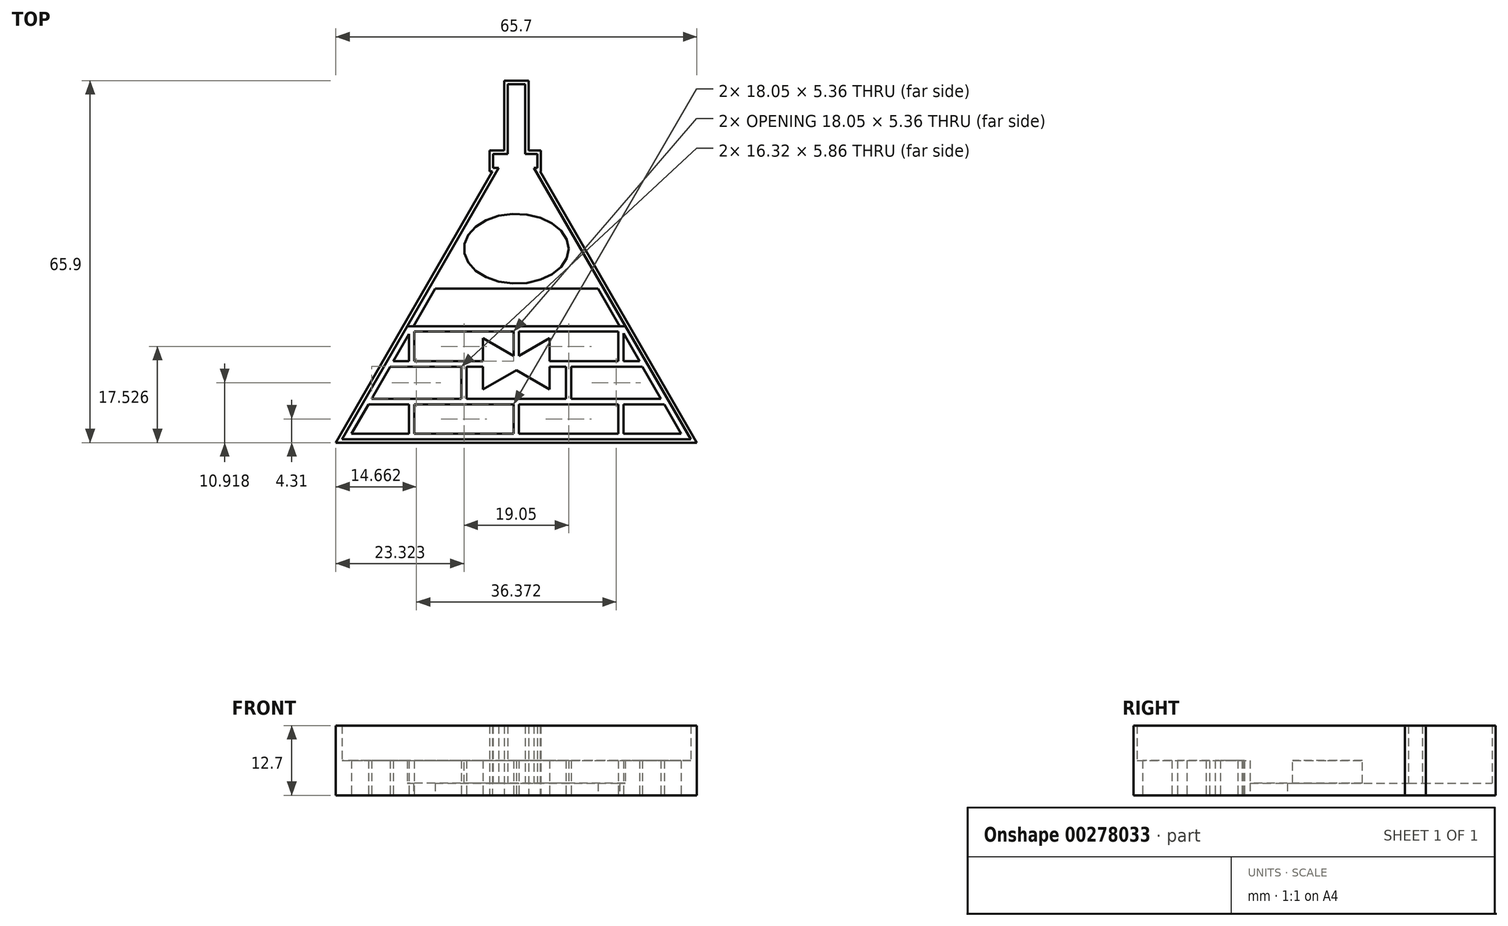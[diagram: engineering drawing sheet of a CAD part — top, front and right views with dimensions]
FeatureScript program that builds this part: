
annotation { "Feature Type Name" : "Feature", "Feature Type Description" : "" }
export const myFeature = defineFeature(function(context is Context, id is Id, definition is map)
    precondition{}
    {
        {
            var Q0;
            Q0=qCreatedBy(makeId("Top.planeOp"),FACE);
            var sketch = newSketch(context, id + "F0", { "sketchPlane" : qUnion([Q0])});
            skLineSegment(sketch, "E0", {"start": v(-57.59, 40.25) * mm, "end": v(-86.1, -9.14) * mm});
            skLineSegment(sketch, "E1", {"start": v(-86.1, -9.14) * mm, "end": v(-22.6, -9.14) * mm});
            skLineSegment(sketch, "E2", {"start": v(-22.6, -9.14) * mm, "end": v(-51.12, 40.25) * mm});
            skEllipse(sketch, "E3", {"center": v(-54.35, 25.53) * mm, "majorRadius": 6.35 * mm, "minorRadius": 9.53 * mm, "majorAxis": v(0, -1)});
            skPoint(sketch, "E4.startSnap0", {"position": v(-63.88, 25.53) * mm});
            skPoint(sketch, "E4.endSnap0", {"position": v(-63.88, 25.53) * mm});
            skLineSegment(sketch, "E5", {"start": v(-74.22, 11.44) * mm, "end": v(-34.48, 11.44) * mm});
            skLineSegment(sketch, "E6", {"start": v(-82.14, -2.28) * mm, "end": v(-26.56, -2.28) * mm});
            skLineSegment(sketch, "E7", {"start": v(-73.4, 11.44) * mm, "end": v(-73.4, 4.58) * mm});
            skLineSegment(sketch, "E8", {"start": v(-35.3, 11.44) * mm, "end": v(-35.3, 4.58) * mm});
            skLineSegment(sketch, "E9", {"start": v(-63.88, 4.58) * mm, "end": v(-63.88, -2.28) * mm});
            skLineSegment(sketch, "E10", {"start": v(-44.83, 4.58) * mm, "end": v(-44.83, -2.28) * mm});
            skLineSegment(sketch, "E11.trimOffspring", {"start": v(-35.3, -2.28) * mm, "end": v(-35.3, -9.14) * mm});
            skLineSegment(sketch, "E12.trimOffspring", {"start": v(-54.35, -2.28) * mm, "end": v(-54.35, -9.14) * mm});
            skLineSegment(sketch, "E13.bottom", {"start": v(-54.35, 29.34) * mm, "end": v(-54.35, 29.34) * mm});
            skLineSegment(sketch, "E13.top", {"start": v(-54.35, 21.72) * mm, "end": v(-54.35, 21.72) * mm});
            skLineSegment(sketch, "E13.left", {"start": v(-54.86, 28.84) * mm, "end": v(-54.86, 22.23) * mm});
            skLineSegment(sketch, "E13.right", {"start": v(-53.84, 28.84) * mm, "end": v(-53.84, 22.23) * mm});
            skPoint(sketch, "E14.visualSharp", {"position": v(-54.86, 29.34) * mm});
            skArc(sketch, "E14.filletArc", {"start": v(-54.35, 29.34) * mm, "mid": v(-54.71, 29.2) * mm, "end": v(-54.86, 28.84) * mm});
            skPoint(sketch, "E15.visualSharp", {"position": v(-53.84, 29.34) * mm});
            skArc(sketch, "E15.filletArc", {"start": v(-53.84, 28.84) * mm, "mid": v(-54, 29.2) * mm, "end": v(-54.35, 29.34) * mm});
            skPoint(sketch, "E16.visualSharp", {"position": v(-54.86, 21.72) * mm});
            skArc(sketch, "E16.filletArc", {"start": v(-54.86, 22.23) * mm, "mid": v(-54.71, 21.87) * mm, "end": v(-54.35, 21.72) * mm});
            skPoint(sketch, "E17.visualSharp", {"position": v(-53.84, 21.72) * mm});
            skArc(sketch, "E17.filletArc", {"start": v(-54.35, 21.72) * mm, "mid": v(-54, 21.87) * mm, "end": v(-53.84, 22.23) * mm});
            skLineSegment(sketch, "E18.trimOffspring", {"start": v(-59.41, 4.58) * mm, "end": v(-78.18, 4.58) * mm});
            skLineSegment(sketch, "E19.bottom", {"start": v(-58.55, 40.25) * mm, "end": v(-57.59, 40.25) * mm});
            skLineSegment(sketch, "E19.top", {"start": v(-58.55, 42.8) * mm, "end": v(-55.94, 42.8) * mm});
            skLineSegment(sketch, "E19.left", {"start": v(-58.55, 40.25) * mm, "end": v(-58.55, 42.8) * mm});
            skLineSegment(sketch, "E19.right", {"start": v(-50.54, 40.25) * mm, "end": v(-50.54, 42.8) * mm});
            skLineSegment(sketch, "E20.top", {"start": v(-55.94, 55.5) * mm, "end": v(-52.76, 55.5) * mm});
            skLineSegment(sketch, "E20.left", {"start": v(-55.94, 42.8) * mm, "end": v(-55.94, 55.5) * mm});
            skLineSegment(sketch, "E20.right", {"start": v(-52.76, 42.8) * mm, "end": v(-52.76, 55.5) * mm});
            skPoint(sketch, "E21.orphan", {"position": v(-54.35, 45.85) * mm});
            skPoint(sketch, "E4.start.orphan", {"position": v(-42.62, 25.53) * mm});
            skPoint(sketch, "E22.trimOffspring.end.orphan", {"position": v(-66.08, 25.53) * mm});
            skLineSegment(sketch, "E23.trimOffspring", {"start": v(-51.12, 40.25) * mm, "end": v(-50.54, 40.25) * mm});
            skLineSegment(sketch, "E24.trimOffspring", {"start": v(-52.76, 42.8) * mm, "end": v(-50.54, 42.8) * mm});
            skLineSegment(sketch, "E25", {"start": v(-81.28, -2.78) * mm, "end": v(-73.9, -2.78) * mm});
            skLineSegment(sketch, "E26", {"start": v(-27.43, -2.78) * mm, "end": v(-24.33, -8.14) * mm});
            skLineSegment(sketch, "E27", {"start": v(-24.33, -8.14) * mm, "end": v(-34.8, -8.14) * mm});
            skLineSegment(sketch, "E28", {"start": v(-84.37, -8.14) * mm, "end": v(-81.28, -2.78) * mm});
            skLineSegment(sketch, "E29", {"start": v(-73.9, -2.78) * mm, "end": v(-73.9, -8.14) * mm});
            skLineSegment(sketch, "E30", {"start": v(-72.9, -2.78) * mm, "end": v(-72.9, -8.14) * mm});
            skLineSegment(sketch, "E31", {"start": v(-54.85, -2.78) * mm, "end": v(-54.85, -8.14) * mm});
            skLineSegment(sketch, "E32", {"start": v(-53.85, -2.78) * mm, "end": v(-53.85, -8.14) * mm});
            skLineSegment(sketch, "E33", {"start": v(-35.8, -2.78) * mm, "end": v(-35.8, -8.14) * mm});
            skLineSegment(sketch, "E34", {"start": v(-34.8, -2.78) * mm, "end": v(-34.8, -8.14) * mm});
            skLineSegment(sketch, "E35.trimOffspring", {"start": v(-72.9, -2.78) * mm, "end": v(-54.85, -2.78) * mm});
            skLineSegment(sketch, "E36.trimOffspring", {"start": v(-73.9, -8.14) * mm, "end": v(-84.37, -8.14) * mm});
            skPoint(sketch, "E37.trimOffspring.end.orphan", {"position": v(-73.4, -9.14) * mm});
            skPoint(sketch, "E37.trimOffspring.start.orphan", {"position": v(-73.4, -2.28) * mm});
            skLineSegment(sketch, "E38", {"start": v(-73.4, -2.28) * mm, "end": v(-73.4, -9.14) * mm});
            skLineSegment(sketch, "E39.trimOffspring", {"start": v(-53.85, -2.78) * mm, "end": v(-35.8, -2.78) * mm});
            skLineSegment(sketch, "E40.trimOffspring", {"start": v(-54.85, -8.14) * mm, "end": v(-72.9, -8.14) * mm});
            skLineSegment(sketch, "E41.trimOffspring", {"start": v(-34.8, -2.78) * mm, "end": v(-27.43, -2.78) * mm});
            skLineSegment(sketch, "E42.trimOffspring", {"start": v(-35.8, -8.14) * mm, "end": v(-53.85, -8.14) * mm});
            skLineSegment(sketch, "E43", {"start": v(-80.7, -1.78) * mm, "end": v(-64.38, -1.78) * mm});
            skLineSegment(sketch, "E44", {"start": v(-28, -1.78) * mm, "end": v(-31.39, 4.08) * mm});
            skLineSegment(sketch, "E45", {"start": v(-31.39, 4.08) * mm, "end": v(-44.33, 4.08) * mm});
            skLineSegment(sketch, "E46", {"start": v(-48.3, 4.08) * mm, "end": v(-48.3, -0.08) * mm});
            skLineSegment(sketch, "E47", {"start": v(-48.3, -0.08) * mm, "end": v(-54.35, 3.42) * mm});
            skLineSegment(sketch, "E48", {"start": v(-54.35, 3.42) * mm, "end": v(-60.41, -0.08) * mm});
            skLineSegment(sketch, "E49", {"start": v(-60.41, -0.08) * mm, "end": v(-60.41, 4.08) * mm});
            skLineSegment(sketch, "E50", {"start": v(-60.41, 4.08) * mm, "end": v(-63.38, 4.08) * mm});
            skLineSegment(sketch, "E51", {"start": v(-77.32, 4.08) * mm, "end": v(-80.7, -1.78) * mm});
            skLineSegment(sketch, "E52", {"start": v(-64.38, -1.78) * mm, "end": v(-64.38, 4.08) * mm});
            skLineSegment(sketch, "E53", {"start": v(-63.38, 4.08) * mm, "end": v(-63.38, -1.78) * mm});
            skLineSegment(sketch, "E54", {"start": v(-45.33, 4.08) * mm, "end": v(-45.33, -1.78) * mm});
            skLineSegment(sketch, "E55", {"start": v(-44.33, 4.08) * mm, "end": v(-44.33, -1.78) * mm});
            skLineSegment(sketch, "E56.trimOffspring", {"start": v(-64.38, 4.08) * mm, "end": v(-77.32, 4.08) * mm});
            skLineSegment(sketch, "E57.trimOffspring", {"start": v(-63.38, -1.78) * mm, "end": v(-45.33, -1.78) * mm});
            skLineSegment(sketch, "E58.trimOffspring", {"start": v(-44.33, -1.78) * mm, "end": v(-28, -1.78) * mm});
            skLineSegment(sketch, "E59.trimOffspring", {"start": v(-45.33, 4.08) * mm, "end": v(-48.3, 4.08) * mm});
            skLineSegment(sketch, "E60", {"start": v(-31.88, 5.08) * mm, "end": v(-34.8, 5.08) * mm});
            skLineSegment(sketch, "E61", {"start": v(-48.3, 5.08) * mm, "end": v(-48.3, 9.23) * mm});
            skLineSegment(sketch, "E62", {"start": v(-60.41, 5.08) * mm, "end": v(-72.9, 5.08) * mm});
            skLineSegment(sketch, "E63", {"start": v(-76.74, 5.08) * mm, "end": v(-73.9, 10) * mm});
            skLineSegment(sketch, "E64", {"start": v(-72.9, 10.44) * mm, "end": v(-54.85, 10.44) * mm});
            skLineSegment(sketch, "E65", {"start": v(-34.8, 10.14) * mm, "end": v(-31.88, 5.08) * mm});
            skLineSegment(sketch, "E66", {"start": v(-34.8, 5.08) * mm, "end": v(-34.8, 10.14) * mm});
            skLineSegment(sketch, "E67", {"start": v(-35.8, 10.44) * mm, "end": v(-35.8, 5.08) * mm});
            skLineSegment(sketch, "E68", {"start": v(-53.85, 6.02) * mm, "end": v(-53.85, 10.44) * mm});
            skLineSegment(sketch, "E69", {"start": v(-54.85, 10.44) * mm, "end": v(-54.85, 6.02) * mm});
            skLineSegment(sketch, "E70", {"start": v(-72.9, 10.44) * mm, "end": v(-72.9, 5.08) * mm});
            skLineSegment(sketch, "E71.trimOffspring", {"start": v(-35.8, 5.08) * mm, "end": v(-48.3, 5.08) * mm});
            skLineSegment(sketch, "E72.trimOffspring", {"start": v(-53.85, 10.44) * mm, "end": v(-35.8, 10.44) * mm});
            skLineSegment(sketch, "E73", {"start": v(-53.85, 6.02) * mm, "end": v(-48.3, 9.23) * mm});
            skLineSegment(sketch, "E74", {"start": v(-60.41, 5.08) * mm, "end": v(-60.41, 9.23) * mm});
            skLineSegment(sketch, "E75", {"start": v(-60.41, 9.23) * mm, "end": v(-54.85, 6.02) * mm});
            skLineSegment(sketch, "E76", {"start": v(-73.9, 10) * mm, "end": v(-73.9, 5.08) * mm});
            skLineSegment(sketch, "E77.trimOffspring", {"start": v(-73.9, 5.08) * mm, "end": v(-76.74, 5.08) * mm});
            skFitSpline(sketch, "E78.0", {"points": [v(-45.92, 24.58) * mm, v(-45.78, 25.53) * mm, v(-45.92, 26.49) * mm, v(-46.35, 27.44) * mm, v(-47.1, 28.37) * mm, v(-48.13, 29.21) * mm, v(-49.43, 29.93) * mm, v(-50.95, 30.47) * mm, v(-52.33, 30.75) * mm, v(-53.48, 30.86) * mm, v(-54.35, 30.9) * mm, v(-55.23, 30.86) * mm, v(-56.37, 30.75) * mm, v(-57.75, 30.47) * mm, v(-59.28, 29.93) * mm, v(-60.58, 29.21) * mm, v(-61.61, 28.37) * mm, v(-62.36, 27.44) * mm, v(-62.78, 26.49) * mm, v(-62.92, 25.53) * mm, v(-62.78, 24.58) * mm, v(-62.36, 23.63) * mm, v(-61.61, 22.7) * mm, v(-60.58, 21.85) * mm, v(-59.28, 21.14) * mm, v(-57.75, 20.6) * mm, v(-56.37, 20.32) * mm, v(-55.23, 20.2) * mm, v(-54.35, 20.17) * mm, v(-53.48, 20.2) * mm, v(-52.33, 20.32) * mm, v(-50.95, 20.6) * mm, v(-49.43, 21.14) * mm, v(-48.13, 21.85) * mm, v(-47.1, 22.7) * mm, v(-46.35, 23.63) * mm, v(-45.92, 24.58) * mm, v(-45.78, 25.53) * mm, v(-45.92, 26.49) * mm, v(-45.92, 24.58) * mm]});
            skLineSegment(sketch, "E79", {"start": v(-69.13, 18.26) * mm, "end": v(-39.49, 18.26) * mm});
            skLineSegment(sketch, "E80.0", {"start": v(-56.57, 43.43) * mm, "end": v(-56.57, 56.13) * mm});
            skLineSegment(sketch, "E80.1", {"start": v(-50.02, 39.62) * mm, "end": v(-49.9, 39.62) * mm});
            skLineSegment(sketch, "E80.2", {"start": v(-49.9, 39.62) * mm, "end": v(-49.9, 43.43) * mm});
            skLineSegment(sketch, "E80.3", {"start": v(-52.13, 43.43) * mm, "end": v(-49.9, 43.43) * mm});
            skLineSegment(sketch, "E80.4", {"start": v(-52.13, 43.43) * mm, "end": v(-52.13, 56.13) * mm});
            skLineSegment(sketch, "E80.5", {"start": v(-21.5, -9.77) * mm, "end": v(-50.02, 39.62) * mm});
            skLineSegment(sketch, "E80.6", {"start": v(-56.57, 56.13) * mm, "end": v(-52.13, 56.13) * mm});
            skLineSegment(sketch, "E80.7", {"start": v(-87.2, -9.77) * mm, "end": v(-21.5, -9.77) * mm});
            skLineSegment(sketch, "E80.8", {"start": v(-58.69, 39.62) * mm, "end": v(-87.2, -9.77) * mm});
            skLineSegment(sketch, "E80.9", {"start": v(-59.18, 39.62) * mm, "end": v(-58.69, 39.62) * mm});
            skLineSegment(sketch, "E80.10", {"start": v(-59.18, 39.62) * mm, "end": v(-59.18, 43.43) * mm});
            skLineSegment(sketch, "E80.11", {"start": v(-59.18, 43.43) * mm, "end": v(-56.57, 43.43) * mm});
            skLineSegment(sketch, "E81", {"start": v(-39.49, 18.26) * mm, "end": v(-35.55, 11.44) * mm});
            skLineSegment(sketch, "E82", {"start": v(-69.13, 18.26) * mm, "end": v(-73.07, 11.44) * mm});
            skSolve(sketch);
        }
        {
            var Q0;
            {var subQ0=sQuery(id+"F0.wireOp",EDGE,"E9");Q0=makeQuery(id+"F0.imprint","IMPRINT",FACE,{"disambiguationData":[TD([[makeQuery(id+"F0.imprint","IMPRINT",EDGE,{"derivedFrom":subQ0}),-1.0]])]});}
            var Q1;
            Q1=makeQuery(id+"F0.imprint","IMPRINT",FACE,{"disambiguationData":[TD([[makeQuery(id+"F0.imprint","IMPRINT",EDGE,{"derivedFrom":sQuery(id+"F0.wireOp",EDGE,"E25")}),1.0]])]});
            var Q2;
            {var subQ0=sQuery(id+"F0.wireOp",EDGE,"E12.trimOffspring");Q2=makeQuery(id+"F0.imprint","IMPRINT",FACE,{"disambiguationData":[TD([[makeQuery(id+"F0.imprint","IMPRINT",EDGE,{"derivedFrom":subQ0}),-1.0]])]});}
            var Q3;
            {var subQ7=sQuery(id+"F0.wireOp",EDGE,"E7");Q3=makeQuery(id+"F0.imprint","IMPRINT",FACE,{"disambiguationData":[TD([[makeQuery(id+"F0.imprint","IMPRINT",EDGE,{"derivedFrom":subQ7}),1.0]])]});}
            var Q4;
            {var subQ1=sQuery(id+"F0.wireOp",EDGE,"E7");Q4=makeQuery(id+"F0.imprint","IMPRINT",FACE,{"disambiguationData":[TD([[makeQuery(id+"F0.imprint","IMPRINT",EDGE,{"derivedFrom":subQ1}),-1.0]])]});}
            var Q5;
            {var subQ3=sQuery(id+"F0.wireOp",EDGE,"E8");Q5=makeQuery(id+"F0.imprint","IMPRINT",FACE,{"disambiguationData":[TD([[makeQuery(id+"F0.imprint","IMPRINT",EDGE,{"derivedFrom":subQ3}),1.0]])]});}
            var Q6;
            {var subQ0=sQuery(id+"F0.wireOp",EDGE,"E10");Q6=makeQuery(id+"F0.imprint","IMPRINT",FACE,{"disambiguationData":[TD([[makeQuery(id+"F0.imprint","IMPRINT",EDGE,{"derivedFrom":subQ0}),1.0]])]});}
            var Q7;
            {var subQ0=sQuery(id+"F0.wireOp",EDGE,"E11.trimOffspring");Q7=makeQuery(id+"F0.imprint","IMPRINT",FACE,{"disambiguationData":[TD([[makeQuery(id+"F0.imprint","IMPRINT",EDGE,{"derivedFrom":subQ0}),1.0]])]});}
            var Q8;
            {var subQ0=sQuery(id+"F0.wireOp",EDGE,"E11.trimOffspring");Q8=makeQuery(id+"F0.imprint","IMPRINT",FACE,{"disambiguationData":[TD([[makeQuery(id+"F0.imprint","IMPRINT",EDGE,{"derivedFrom":subQ0}),-1.0]])]});}
            var Q9;
            Q9=makeQuery(id+"F0.imprint","IMPRINT",FACE,{"disambiguationData":[TD([[makeQuery(id+"F0.imprint","IMPRINT",EDGE,{"derivedFrom":sQuery(id+"F0.wireOp",EDGE,"E3")}),1.0]])]});
            var Q10;
            Q10=makeQuery(id+"F0.imprint","IMPRINT",FACE,{"disambiguationData":[TD([[makeQuery(id+"F0.imprint","IMPRINT",EDGE,{"derivedFrom":sQuery(id+"F0.wireOp",EDGE,"E13.left")}),1.0]])]});
            extrude(context, id + "F1", {"entities" : qUnion([Q0, Q1, Q2, Q3, Q4, Q5, Q6, Q7, Q8, Q9, Q10]), "depth" : 6.35 * mm});
        }
        {
            var Q0;
            {var subQ1=sQuery(id+"F0.wireOp",EDGE,"E19.bottom");Q0=makeQuery(id+"F0.imprint","IMPRINT",FACE,{"disambiguationData":[TD([[makeQuery(id+"F0.imprint","IMPRINT",EDGE,{"derivedFrom":subQ1}),-1.0]])]});}
            extrude(context, id + "F2", {"entities" : qUnion([Q0]), "operationType" : NewBodyOperationType.ADD, "depth" : 12.7 * mm});
        }
        {
            var Q0;
            Q0=makeQuery(id+"F0.imprint","IMPRINT",FACE,{"disambiguationData":[TD([[makeQuery(id+"F0.imprint","IMPRINT",EDGE,{"derivedFrom":sQuery(id+"F0.wireOp",EDGE,"E3")}),-1.0]])]});
            var Q1;
            Q1=makeQuery(id+"F0.imprint","IMPRINT",FACE,{"disambiguationData":[TD([[makeQuery(id+"F0.imprint","IMPRINT",EDGE,{"derivedFrom":sQuery(id+"F0.wireOp",EDGE,"E3")}),1.0]])]});
            var Q2;
            Q2=makeQuery(id+"F0.imprint","IMPRINT",FACE,{"disambiguationData":[TD([[makeQuery(id+"F0.imprint","IMPRINT",EDGE,{"derivedFrom":sQuery(id+"F0.wireOp",EDGE,"E13.left")}),-1.0]])]});
            var Q3;
            Q3=makeQuery(id+"F0.imprint","IMPRINT",FACE,{"disambiguationData":[TD([[makeQuery(id+"F0.imprint","IMPRINT",EDGE,{"derivedFrom":sQuery(id+"F0.wireOp",EDGE,"E13.left")}),1.0]])]});
            extrude(context, id + "F3", {"entities" : qUnion([Q0, Q1, Q2, Q3]), "operationType" : NewBodyOperationType.ADD, "depth" : 2.2 * mm});
        }
    });
